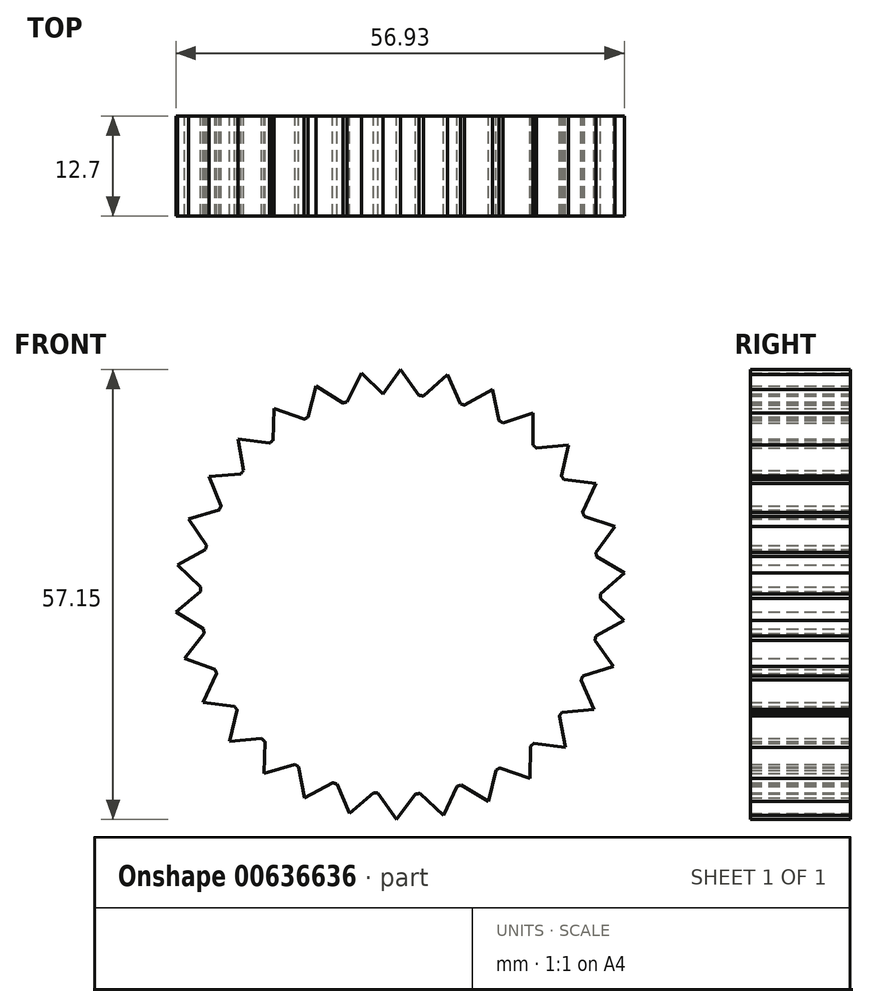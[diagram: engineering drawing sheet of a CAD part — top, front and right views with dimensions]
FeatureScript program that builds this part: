
annotation { "Feature Type Name" : "Feature", "Feature Type Description" : "" }
export const myFeature = defineFeature(function(context is Context, id is Id, definition is map)
    precondition{}
    {
        {
            var Q0;
            Q0=qCreatedBy(makeId("Front.planeOp"),FACE);
            var sketch = newSketch(context, id + "F0", { "sketchPlane" : qUnion([Q0])});
            skCircle(sketch, "E0", {"center": v(0, 0) * mm, "radius": 25.4 * mm});
            skLineSegment(sketch, "E1", {"start": v(0, 25.4) * mm, "end": v(0, 28.58) * mm, "construction": true});
            skLineSegment(sketch, "E2", {"start": v(0, 28.58) * mm, "end": v(-2.39, 25.29) * mm});
            skLineSegment(sketch, "E3.MirrorCS", {"start": v(0, 28.58) * mm, "end": v(2.39, 25.29) * mm});
            skLineSegment(sketch, "E4.1.0", {"start": v(5.97, 27.94) * mm, "end": v(2.95, 25.23) * mm});
            skLineSegment(sketch, "E4.1.1", {"start": v(5.97, 27.94) * mm, "end": v(7.62, 24.23) * mm});
            skLineSegment(sketch, "E4.2.0", {"start": v(11.69, 26.08) * mm, "end": v(8.16, 24.05) * mm});
            skLineSegment(sketch, "E4.2.1", {"start": v(11.69, 26.08) * mm, "end": v(12.52, 22.1) * mm});
            skLineSegment(sketch, "E4.3.0", {"start": v(16.88, 23.06) * mm, "end": v(13, 21.82) * mm});
            skLineSegment(sketch, "E4.3.1", {"start": v(16.88, 23.06) * mm, "end": v(16.87, 19) * mm});
            skLineSegment(sketch, "E4.4.0", {"start": v(21.33, 19.02) * mm, "end": v(17.28, 18.61) * mm});
            skLineSegment(sketch, "E4.4.1", {"start": v(21.33, 19.02) * mm, "end": v(20.46, 15.05) * mm});
            skLineSegment(sketch, "E4.5.0", {"start": v(24.83, 14.14) * mm, "end": v(20.8, 14.59) * mm});
            skLineSegment(sketch, "E4.5.1", {"start": v(24.83, 14.14) * mm, "end": v(23.16, 10.44) * mm});
            skLineSegment(sketch, "E4.6.0", {"start": v(27.24, 8.63) * mm, "end": v(23.38, 9.92) * mm});
            skLineSegment(sketch, "E4.6.1", {"start": v(27.24, 8.63) * mm, "end": v(24.83, 5.36) * mm});
            skLineSegment(sketch, "E4.7.0", {"start": v(28.44, 2.75) * mm, "end": v(24.94, 4.8) * mm});
            skLineSegment(sketch, "E4.7.1", {"start": v(28.44, 2.75) * mm, "end": v(25.4, 0.05) * mm});
            skLineSegment(sketch, "E4.8.0", {"start": v(28.39, -3.26) * mm, "end": v(25.4, -0.51) * mm});
            skLineSegment(sketch, "E4.8.1", {"start": v(28.39, -3.26) * mm, "end": v(24.85, -5.26) * mm});
            skLineSegment(sketch, "E4.9.0", {"start": v(27.08, -9.12) * mm, "end": v(24.73, -5.81) * mm});
            skLineSegment(sketch, "E4.9.1", {"start": v(27.08, -9.12) * mm, "end": v(23.2, -10.34) * mm});
            skLineSegment(sketch, "E4.10.0", {"start": v(24.57, -14.58) * mm, "end": v(22.97, -10.85) * mm});
            skLineSegment(sketch, "E4.10.1", {"start": v(24.57, -14.58) * mm, "end": v(20.53, -14.96) * mm});
            skLineSegment(sketch, "E4.11.0", {"start": v(20.98, -19.4) * mm, "end": v(20.19, -15.41) * mm});
            skLineSegment(sketch, "E4.11.1", {"start": v(20.98, -19.4) * mm, "end": v(16.94, -18.92) * mm});
            skLineSegment(sketch, "E4.12.0", {"start": v(16.46, -23.36) * mm, "end": v(16.52, -19.3) * mm});
            skLineSegment(sketch, "E4.12.1", {"start": v(16.46, -23.36) * mm, "end": v(12.61, -22.05) * mm});
            skLineSegment(sketch, "E4.13.0", {"start": v(11.21, -26.28) * mm, "end": v(12.12, -22.32) * mm});
            skLineSegment(sketch, "E4.13.1", {"start": v(11.21, -26.28) * mm, "end": v(7.73, -24.2) * mm});
            skLineSegment(sketch, "E4.14.0", {"start": v(5.47, -28.05) * mm, "end": v(7.18, -24.36) * mm});
            skLineSegment(sketch, "E4.14.1", {"start": v(5.47, -28.05) * mm, "end": v(2.5, -25.28) * mm});
            skLineSegment(sketch, "E4.15.0", {"start": v(-0.52, -28.57) * mm, "end": v(1.93, -25.33) * mm});
            skLineSegment(sketch, "E4.15.1", {"start": v(-0.52, -28.57) * mm, "end": v(-2.85, -25.24) * mm});
            skLineSegment(sketch, "E4.16.0", {"start": v(-6.48, -27.83) * mm, "end": v(-3.4, -25.17) * mm});
            skLineSegment(sketch, "E4.16.1", {"start": v(-6.48, -27.83) * mm, "end": v(-8.06, -24.09) * mm});
            skLineSegment(sketch, "E4.17.0", {"start": v(-12.15, -25.86) * mm, "end": v(-8.6, -23.9) * mm});
            skLineSegment(sketch, "E4.17.1", {"start": v(-12.15, -25.86) * mm, "end": v(-12.92, -21.87) * mm});
            skLineSegment(sketch, "E4.18.0", {"start": v(-17.3, -22.75) * mm, "end": v(-13.4, -21.58) * mm});
            skLineSegment(sketch, "E4.18.1", {"start": v(-17.3, -22.75) * mm, "end": v(-17.2, -18.69) * mm});
            skLineSegment(sketch, "E4.19.0", {"start": v(-21.67, -18.63) * mm, "end": v(-17.62, -18.3) * mm});
            skLineSegment(sketch, "E4.19.1", {"start": v(-21.67, -18.63) * mm, "end": v(-20.73, -14.67) * mm});
            skLineSegment(sketch, "E4.20.0", {"start": v(-25.08, -13.69) * mm, "end": v(-21.05, -14.21) * mm});
            skLineSegment(sketch, "E4.20.1", {"start": v(-25.08, -13.69) * mm, "end": v(-23.34, -10.02) * mm});
            skLineSegment(sketch, "E4.21.0", {"start": v(-27.4, -8.14) * mm, "end": v(-23.56, -9.5) * mm});
            skLineSegment(sketch, "E4.21.1", {"start": v(-27.4, -8.14) * mm, "end": v(-24.92, -4.91) * mm});
            skLineSegment(sketch, "E4.22.0", {"start": v(-28.49, -2.23) * mm, "end": v(-25.02, -4.36) * mm});
            skLineSegment(sketch, "E4.22.1", {"start": v(-28.49, -2.23) * mm, "end": v(-25.4, 0.4) * mm});
            skLineSegment(sketch, "E4.23.0", {"start": v(-28.32, 3.77) * mm, "end": v(-25.38, 0.97) * mm});
            skLineSegment(sketch, "E4.23.1", {"start": v(-28.32, 3.77) * mm, "end": v(-24.75, 5.7) * mm});
            skLineSegment(sketch, "E4.24.0", {"start": v(-26.91, 9.61) * mm, "end": v(-24.62, 6.26) * mm});
            skLineSegment(sketch, "E4.24.1", {"start": v(-26.91, 9.61) * mm, "end": v(-23.01, 10.76) * mm});
            skLineSegment(sketch, "E4.25.0", {"start": v(-24.3, 15.03) * mm, "end": v(-22.77, 11.26) * mm});
            skLineSegment(sketch, "E4.25.1", {"start": v(-24.3, 15.03) * mm, "end": v(-20.25, 15.33) * mm});
            skLineSegment(sketch, "E4.26.0", {"start": v(-20.63, 19.78) * mm, "end": v(-19.9, 15.78) * mm});
            skLineSegment(sketch, "E4.26.1", {"start": v(-20.63, 19.78) * mm, "end": v(-16.6, 19.22) * mm});
            skLineSegment(sketch, "E4.27.0", {"start": v(-16.04, 23.65) * mm, "end": v(-16.17, 19.59) * mm});
            skLineSegment(sketch, "E4.27.1", {"start": v(-16.04, 23.65) * mm, "end": v(-12.21, 22.27) * mm});
            skLineSegment(sketch, "E4.28.0", {"start": v(-10.74, 26.48) * mm, "end": v(-11.72, 22.54) * mm});
            skLineSegment(sketch, "E4.28.1", {"start": v(-10.74, 26.48) * mm, "end": v(-7.29, 24.33) * mm});
            skLineSegment(sketch, "E4.29.0", {"start": v(-4.96, 28.14) * mm, "end": v(-6.74, 24.49) * mm});
            skLineSegment(sketch, "E4.29.1", {"start": v(-4.96, 28.14) * mm, "end": v(-2.04, 25.32) * mm});
            skLineSegment(sketch, "E4.anchor1", {"start": v(0, 0) * mm, "end": v(-2.39, 25.29) * mm, "construction": true});
            skLineSegment(sketch, "E4.anchor2", {"start": v(0, 0) * mm, "end": v(-6.74, 24.49) * mm, "construction": true});
            skSolve(sketch);
        }
        {
            var Q0;
            Q0 = qSketchRegion(id + "F0", true);
            extrude(context, id + "F1", {"entities" : qUnion([Q0]), "depth" : 12.7 * mm, "offsetDistance" : 25.4 * mm});
        }
    });
